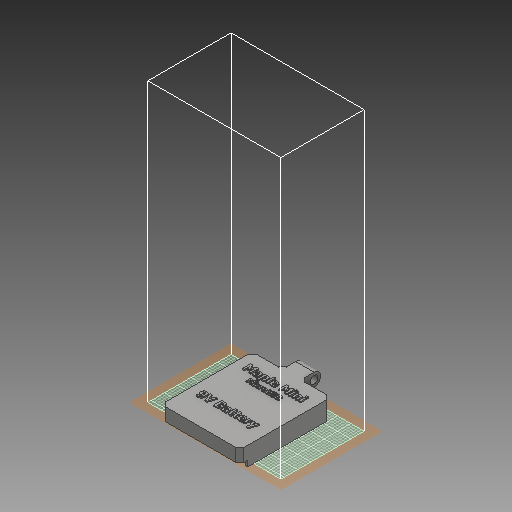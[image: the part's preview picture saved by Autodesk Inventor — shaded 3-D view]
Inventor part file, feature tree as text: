
AUTODESK INVENTOR PART (.ipt)
format: ipt  version: 2018 (Build 220112000, 112)  size: 1,206,272 bytes
history: native  units: in
note: dims shown in document units (in); Inventor stores cm internally (conversion verified against a paired STEP export)
features: extrude x3, sketch x3, move_body x2, chamfer x1, fillet x1, direct_edit x1
ambient origin geometry x8: Origin, YZ Plane, XZ Plane, XY Plane, X Axis, Y Axis, Z Axis, Center Point
bodies: Solid1 (feature_tree)
feature tree (11):
  extrude  "Extrusion1"  Depth=0.35in
  chamfer  "Chamfer1"  Distance=1.723in
  fillet  "Fillet1"  Radius=0.246in
  extrude  "Extrusion2"  Depth=0.11in TaperAngle=45.0deg
  extrude  "Extrusion3"  Depth=0.123in
  direct_edit  "Direct Edit1"
  sketch  "Sketch1"  dims[d0=0.35in d1=0.375in]
  sketch  "Sketch2"  dims[d2=0.57in]
  sketch  "Sketch4"  dims[d3=0.57in d4=1.723in d5=0.246in d6=0.0in d7=0.075in d8=0.125in d9=45.0deg d10=0.123in d11=0.146in d12=0.246in d13=0.0in d16=0.05in d17=0.125in d19=0.11in d20=0.0in d21=0.0in d22=0.0in d23=0.105in d24=0.0in d25=0.0in d26=0.105in]
  move_body  "Move1"
  move_body  "Move2"
